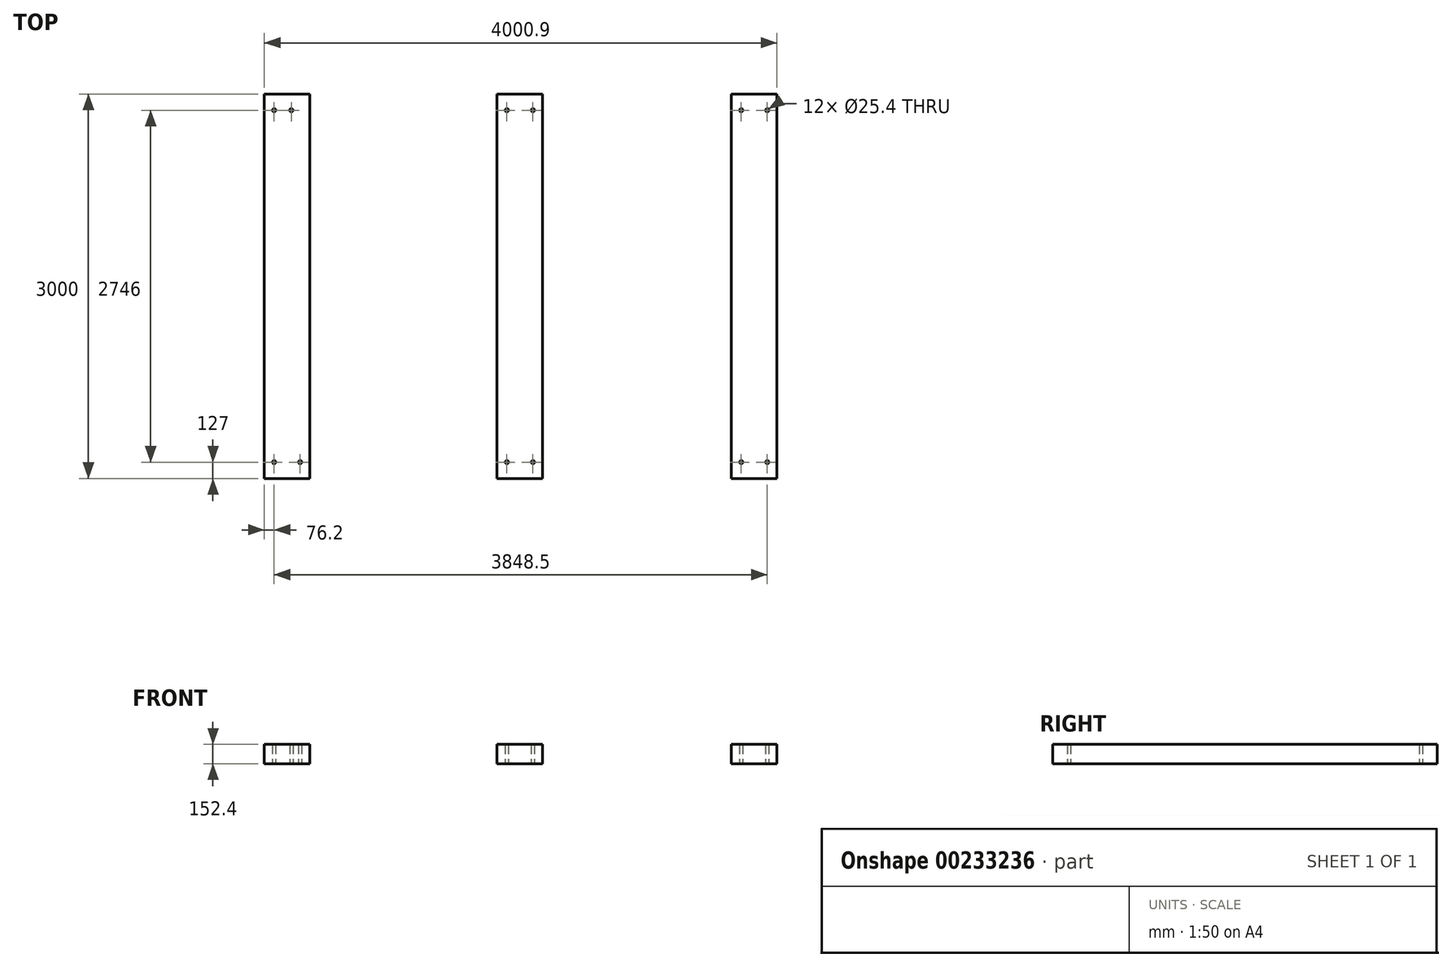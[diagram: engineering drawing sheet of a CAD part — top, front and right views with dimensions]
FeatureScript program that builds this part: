
annotation { "Feature Type Name" : "Feature", "Feature Type Description" : "" }
export const myFeature = defineFeature(function(context is Context, id is Id, definition is map)
    precondition{}
    {
        {
            var Q0;
            Q0=qCreatedBy(makeId("Top.planeOp"),FACE);
            var sketch = newSketch(context, id + "F0", { "sketchPlane" : qUnion([Q0])});
            skLineSegment(sketch, "E0.bottom", {"start": v(-2369.02, 127) * mm, "end": v(-2013.42, 127) * mm});
            skLineSegment(sketch, "E0.top", {"start": v(-2369.02, -2873) * mm, "end": v(-2013.42, -2873) * mm});
            skLineSegment(sketch, "E0.left", {"start": v(-2369.02, 127) * mm, "end": v(-2369.02, -2873) * mm});
            skLineSegment(sketch, "E0.right", {"start": v(-2013.42, 127) * mm, "end": v(-2013.42, -2873) * mm});
            skLineSegment(sketch, "E1.bottom", {"start": v(-552.52, 127) * mm, "end": v(-196.92, 127) * mm});
            skLineSegment(sketch, "E1.top", {"start": v(-552.52, -2873) * mm, "end": v(-196.92, -2873) * mm});
            skLineSegment(sketch, "E1.left", {"start": v(-552.52, 127) * mm, "end": v(-552.52, -2873) * mm});
            skLineSegment(sketch, "E1.right", {"start": v(-196.92, 127) * mm, "end": v(-196.92, -2873) * mm});
            skPoint(sketch, "E2.firstSnap0", {"position": v(-374.72, 127) * mm});
            skLineSegment(sketch, "E2.bottom", {"start": v(1276.28, 127) * mm, "end": v(1631.88, 127) * mm});
            skLineSegment(sketch, "E2.top", {"start": v(1276.28, -2873) * mm, "end": v(1631.88, -2873) * mm});
            skLineSegment(sketch, "E2.left", {"start": v(1276.28, 127) * mm, "end": v(1276.28, -2873) * mm});
            skLineSegment(sketch, "E2.right", {"start": v(1631.88, 127) * mm, "end": v(1631.88, -2873) * mm});
            skCircle(sketch, "E3", {"center": v(-2292.82, 0) * mm, "radius": 12.7 * mm});
            skCircle(sketch, "E4", {"center": v(-2158.08, 0) * mm, "radius": 12.7 * mm});
            skCircle(sketch, "E5", {"center": v(-2292.82, -2746) * mm, "radius": 12.7 * mm});
            skCircle(sketch, "E6", {"center": v(-2089.62, -2746) * mm, "radius": 12.7 * mm});
            skCircle(sketch, "E7", {"center": v(-476.32, 0) * mm, "radius": 12.7 * mm});
            skCircle(sketch, "E8", {"center": v(-273.12, 0) * mm, "radius": 12.7 * mm});
            skCircle(sketch, "E9", {"center": v(-476.32, -2746) * mm, "radius": 12.7 * mm});
            skCircle(sketch, "E10", {"center": v(-273.12, -2746) * mm, "radius": 12.7 * mm});
            skCircle(sketch, "E11", {"center": v(1352.48, 0) * mm, "radius": 12.7 * mm});
            skCircle(sketch, "E12", {"center": v(1555.68, 0) * mm, "radius": 12.7 * mm});
            skCircle(sketch, "E13", {"center": v(1352.48, -2746) * mm, "radius": 12.7 * mm});
            skCircle(sketch, "E14", {"center": v(1555.68, -2746) * mm, "radius": 12.7 * mm});
            skSolve(sketch);
        }
        {
            var Q0;
            Q0 = qSketchRegion(id + "F0", true);
            extrude(context, id + "F1", {"entities" : qUnion([Q0]), "depth" : 152.4 * mm});
        }
    });
